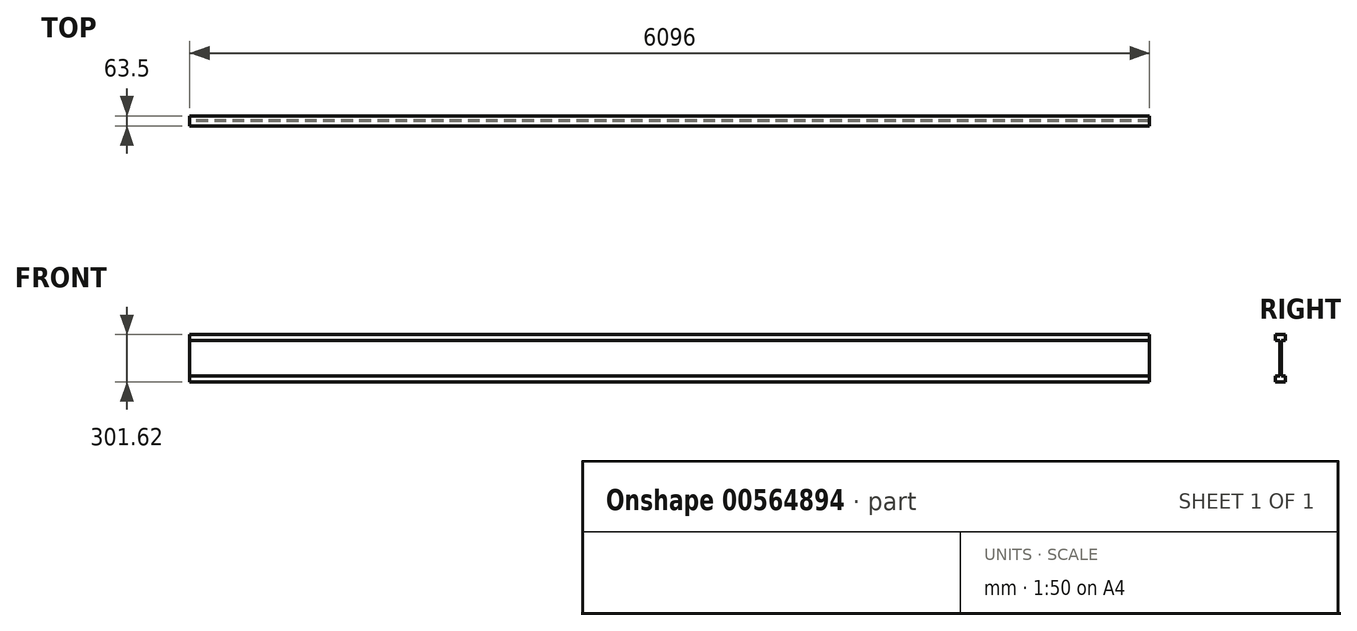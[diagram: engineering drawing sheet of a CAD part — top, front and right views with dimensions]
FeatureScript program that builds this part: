
annotation { "Feature Type Name" : "Feature", "Feature Type Description" : "" }
export const myFeature = defineFeature(function(context is Context, id is Id, definition is map)
    precondition{}
    {
        {
            var Q0;
            Q0=qCreatedBy(makeId("Right.planeOp"),FACE);
            var sketch = newSketch(context, id + "F0", { "sketchPlane" : qUnion([Q0])});
            skLineSegment(sketch, "E0", {"start": v(0, 0) * mm, "end": v(63.5, 0) * mm});
            skLineSegment(sketch, "E1", {"start": v(63.5, 0) * mm, "end": v(63.5, 38.1) * mm});
            skLineSegment(sketch, "E2", {"start": v(63.5, 38.1) * mm, "end": v(36.51, 38.1) * mm});
            skLineSegment(sketch, "E3", {"start": v(36.51, 38.1) * mm, "end": v(36.51, 263.53) * mm});
            skLineSegment(sketch, "E4", {"start": v(36.51, 263.53) * mm, "end": v(63.5, 263.53) * mm});
            skLineSegment(sketch, "E5", {"start": v(63.5, 263.53) * mm, "end": v(63.5, 301.63) * mm});
            skLineSegment(sketch, "E6", {"start": v(63.5, 301.63) * mm, "end": v(0, 301.63) * mm});
            skLineSegment(sketch, "E7", {"start": v(0, 301.63) * mm, "end": v(0, 263.53) * mm});
            skLineSegment(sketch, "E8", {"start": v(0, 263.53) * mm, "end": v(26.99, 263.53) * mm});
            skLineSegment(sketch, "E9", {"start": v(26.99, 263.53) * mm, "end": v(26.99, 38.1) * mm});
            skLineSegment(sketch, "E10", {"start": v(26.99, 38.1) * mm, "end": v(0, 38.1) * mm});
            skLineSegment(sketch, "E11", {"start": v(0, 38.1) * mm, "end": v(0, 0) * mm});
            skSolve(sketch);
        }
        {
            var Q0;
            Q0=qSketchRegion(id+"F0",true);
            extrude(context, id + "F1", {"entities" : qUnion([Q0]), "depth" : 6096 * mm, "offsetDistance" : 25.4 * mm});
        }
    });
